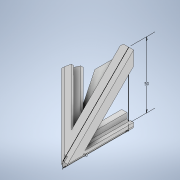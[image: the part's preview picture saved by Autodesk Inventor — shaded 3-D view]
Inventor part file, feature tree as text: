
AUTODESK INVENTOR PART (.ipt)
format: ipt  version: 2020 (Build 240168000, 168)  size: 260,608 bytes
history: native  units: mm
features: sketch x12, extrude x12, pattern_circular x1, revolve x1
ambient origin geometry x8: Origin, YZ Plane, XZ Plane, XY Plane, X Axis, Y Axis, Z Axis, Center Point
bodies: Solid1 (feature_tree)
feature tree (26):
  sketch  "Sketch1"  dims[d0=50.0mm d1=50.0mm]
  extrude  "Extrusion1"  Depth=50.0mm
  extrude  "Extrusion2"  Depth=2.5mm TaperAngle=0.0deg
  pattern_circular  "Circular Pattern1"  Count=2 Angle=90.0deg
  revolve  "Revolution1"  [1 undecoded]
  extrude  "Extrusion3"  Depth=25.0mm TaperAngle=0.0deg
  extrude  "Extrusion4"  Depth=9.0mm TaperAngle=0.0deg
  extrude  "Extrusion5"  Depth=4.0mm TaperAngle=0.0deg
  extrude  "Extrusion6"  Depth=3.0mm TaperAngle=0.0deg
  extrude  "Extrusion7"  [1 undecoded]
  extrude  "Extrusion8"  [1 undecoded]
  extrude  "Extrusion9"  [1 undecoded]
  extrude  "Extrusion10"  [1 undecoded]
  extrude  "Extrusion11"  [1 undecoded]
  extrude  "Extrusion12"  [1 undecoded]
  sketch  "Sketch2"  dims[d2=7.5mm d3=0.0mm d4=2.5mm d5=0.0mm d6=20.0mm d7=90.0deg]
  sketch  "Sketch3"  dims[d9=45.0deg d10=25.0mm d11=0.0mm]
  sketch  "Sketch4"  dims[d12=25.0mm d13=0.0mm d14=25.0mm d15=0.0mm]
  sketch  "Sketch5"  dims[d16=3.0mm d17=0.0mm d18=9.0mm d19=0.0mm]
  sketch  "Sketch6"  dims[d20=9.0mm d21=0.0mm d22=4.0mm d23=0.0mm]
  sketch  "Sketch7"  dims[d24=6.0mm d25=0.0mm d26=3.0mm d27=0.0mm]
  sketch  "Sketch8"  dims[d28=3.0mm d29=0.0mm]
  sketch  "Sketch9"
  sketch  "Sketch10"
  sketch  "Sketch11"
  sketch  "Sketch12"
note: 7 required parameter values undecoded (feature->parameter linkage not recoverable at this tier; creation-order binding heuristic only, values carry confidence <= 0.55)